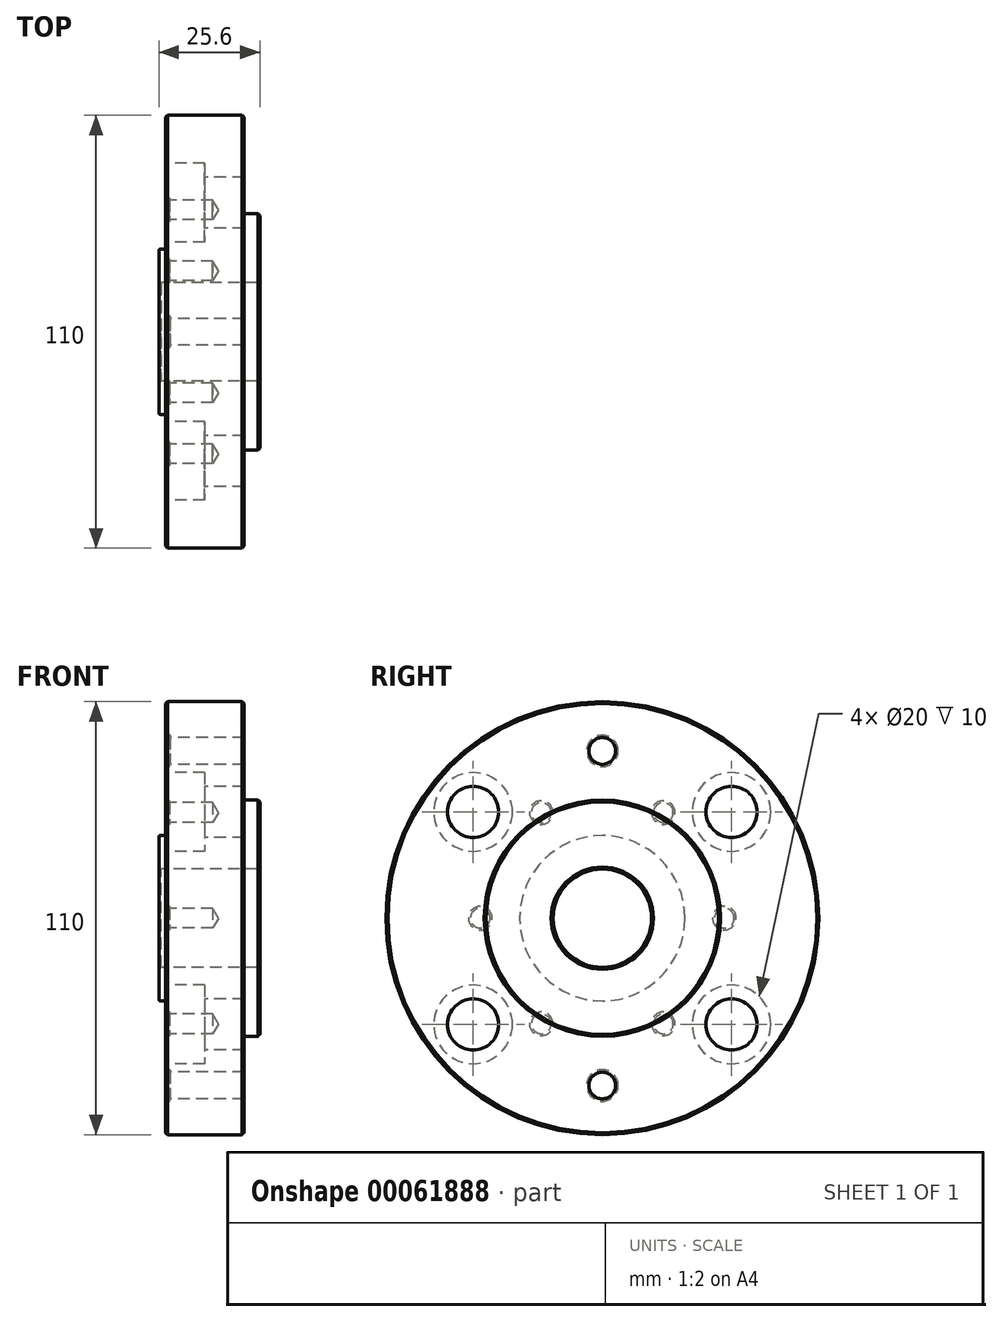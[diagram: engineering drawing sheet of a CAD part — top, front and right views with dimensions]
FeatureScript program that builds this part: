
annotation { "Feature Type Name" : "Feature", "Feature Type Description" : "" }
export const myFeature = defineFeature(function(context is Context, id is Id, definition is map)
    precondition{}
    {
        {
            var Q0;
            Q0=qCreatedBy(makeId("Right.planeOp"),FACE);
            var sketch = newSketch(context, id + "F0", { "sketchPlane" : qUnion([Q0])});
            skCircle(sketch, "E0", {"center": v(0, 0) * mm, "radius": 42.5 * mm, "construction": true});
            skCircle(sketch, "E1", {"center": v(0, 0) * mm, "radius": 21 * mm});
            skCircle(sketch, "E2", {"center": v(0, 0) * mm, "radius": 30 * mm});
            skCircle(sketch, "E3", {"center": v(0, 0) * mm, "radius": 31 * mm, "construction": true});
            skCircle(sketch, "E4", {"center": v(0, 0) * mm, "radius": 55 * mm});
            skPoint(sketch, "E5", {"position": v(-31, 0) * mm});
            skPoint(sketch, "E6", {"position": v(-32.82, -27) * mm});
            skPoint(sketch, "E7", {"position": v(-32.82, 27) * mm});
            skPoint(sketch, "E8", {"position": v(32.82, 27) * mm});
            skPoint(sketch, "E9", {"position": v(32.82, -27) * mm});
            skPoint(sketch, "E10.1.0", {"position": v(-15.5, -26.85) * mm});
            skPoint(sketch, "E10.2.0", {"position": v(15.5, -26.85) * mm});
            skPoint(sketch, "E11.0.3.0", {"position": v(31, 0) * mm});
            skPoint(sketch, "E11.0.4.0", {"position": v(15.5, 26.85) * mm});
            skPoint(sketch, "E11.0.5.0", {"position": v(-15.5, 26.85) * mm});
            skPoint(sketch, "E12", {"position": v(0, -42.5) * mm});
            skPoint(sketch, "E13", {"position": v(0, 42.5) * mm});
            skCircle(sketch, "E14", {"center": v(0, 0) * mm, "radius": 12.5 * mm});
            skSolve(sketch);
        }
        {
            var Q0;
            Q0 = qSketchRegion(id + "F0", true);
            var Q1;
            Q1=makeQuery(id+"F0.imprint","IMPRINT",FACE,{"disambiguationData":[TD([[makeQuery(id+"F0.imprint","IMPRINT",EDGE,{"derivedFrom":sQuery(id+"F0.wireOp",EDGE,"E1")}),1.0]])]});
            var Q2;
            Q2=makeQuery(id+"F0.imprint","IMPRINT",FACE,{"disambiguationData":[TD([[makeQuery(id+"F0.imprint","IMPRINT",EDGE,{"derivedFrom":sQuery(id+"F0.wireOp",EDGE,"E2")}),1.0]])]});
            extrude(context, id + "F1", {"entities" : qUnion([Q0, Q1, Q2]), "depth" : 20 * mm});
        }
        {
            var Q0;
            Q0=makeQuery(id+"F0.imprint","IMPRINT",FACE,{"disambiguationData":[TD([[makeQuery(id+"F0.imprint","IMPRINT",EDGE,{"derivedFrom":sQuery(id+"F0.wireOp",EDGE,"E1")}),1.0]])]});
            var Q1;
            Q1=sQuery(id+"F0.wireOp",EDGE,"E2");
            extrude(context, id + "F2", {"entities" : qUnion([Q0]), "operationType" : NewBodyOperationType.ADD, "surfaceEntities" : qUnion([Q1]), "oppositeDirection" : true, "depth" : 1.6 * mm});
        }
        {
            var Q0;
            Q0=makeQuery(id+"F1.opExtrude","CAP_FACE",FACE,{"disambiguationData":[OSD([sQuery(id+"F0.wireOp",EDGE,"E4")])],"isStart":false});
            var sketch = newSketch(context, id + "F3", { "sketchPlane" : qUnion([Q0])});
            skCircle(sketch, "E15.0", {"center": v(0, 0) * mm, "radius": 30 * mm});
            skSolve(sketch);
        }
        {
            var Q0;
            Q0=makeQuery(id+"F3.imprint","IMPRINT",FACE,{"disambiguationData":[TD([[makeQuery(id+"F3.imprint","IMPRINT",EDGE,{"derivedFrom":sQuery(id+"F3.wireOp",EDGE,"E15.0")}),1.0]])]});
            extrude(context, id + "F4", {"entities" : qUnion([Q0]), "operationType" : NewBodyOperationType.ADD, "depth" : 4 * mm});
        }
        {
            var Q0;
            Q0=sQuery(id+"F0.wireOp",VERTEX,"E11.0.5.0");
            var Q1;
            Q1=sQuery(id+"F0.wireOp",VERTEX,"E5");
            var Q2;
            Q2=sQuery(id+"F0.wireOp",VERTEX,"E10.1.0");
            var Q3;
            Q3=sQuery(id+"F0.wireOp",VERTEX,"E11.0.4.0");
            var Q4;
            Q4=sQuery(id+"F0.wireOp",VERTEX,"E11.0.3.0");
            var Q5;
            Q5=sQuery(id+"F0.wireOp",VERTEX,"E10.2.0");
            var Q6;
            Q6=makeQuery(id+"F1.opExtrude","SWEPT_BODY",BODY,{"disambiguationData":[OSD([sQuery(id+"F0.wireOp",EDGE,"E4")])]});
            hole(context, id + "F5", {"style" : HoleStyle.C_BORE, "holeDiameter" : 5 * mm, "cBoreDiameter" : 6 * mm, "cBoreDepth" : 1 * mm, "endStyle" : HoleEndStyle.BLIND, "oppositeDirection" : true, "holeDepth" : 12 * mm, "locations" : qUnion([Q0, Q1, Q2, Q3, Q4, Q5]), "scope" : qUnion([Q6])});
        }
        {
            var Q0;
            Q0=sQuery(id+"F0.wireOp",VERTEX,"E6");
            var Q1;
            Q1=sQuery(id+"F0.wireOp",VERTEX,"E7");
            var Q2;
            Q2=sQuery(id+"F0.wireOp",VERTEX,"E8");
            var Q3;
            Q3=sQuery(id+"F0.wireOp",VERTEX,"E9");
            var Q4;
            Q4=makeQuery(id+"F1.opExtrude","SWEPT_BODY",BODY,{"disambiguationData":[OSD([sQuery(id+"F0.wireOp",EDGE,"E4")])]});
            hole(context, id + "F6", {"style" : HoleStyle.C_BORE, "holeDiameter" : 13 * mm, "cBoreDiameter" : 20 * mm, "cBoreDepth" : 10 * mm, "endStyle" : HoleEndStyle.THROUGH, "oppositeDirection" : true, "locations" : qUnion([Q0, Q1, Q2, Q3]), "scope" : qUnion([Q4])});
        }
        {
            var Q0;
            Q0=sQuery(id+"F0.wireOp",VERTEX,"E13");
            var Q1;
            Q1=sQuery(id+"F0.wireOp",VERTEX,"E12");
            var Q2;
            Q2=makeQuery(id+"F1.opExtrude","SWEPT_BODY",BODY,{"disambiguationData":[OSD([sQuery(id+"F0.wireOp",EDGE,"E4"),sQuery(id+"F0.wireOp",EDGE,"E14")])]});
            hole(context, id + "F7", {"style" : HoleStyle.C_BORE, "holeDiameter" : 6.8 * mm, "cBoreDiameter" : 8 * mm, "cBoreDepth" : 1.2 * mm, "endStyle" : HoleEndStyle.THROUGH, "oppositeDirection" : true, "locations" : qUnion([Q0, Q1]), "scope" : qUnion([Q2])});
        }
        {
            var Q0;
            Q0=makeQuery(id+"F2.opExtrude","CAP_EDGE",EDGE,{"disambiguationData":[OSD([sQuery(id+"F0.wireOp",EDGE,"E2")])],"isStart":false});
            var Q1;
            Q1=makeQuery(id+"F1.opExtrude","CAP_EDGE",EDGE,{"disambiguationData":[OSD([sQuery(id+"F0.wireOp",EDGE,"E4")])],"isStart":false});
            var Q2;
            Q2=makeQuery(id+"F1.opExtrude","CAP_EDGE",EDGE,{"disambiguationData":[OSD([sQuery(id+"F0.wireOp",EDGE,"E4")])],"isStart":true});
            var Q3;
            Q3=makeQuery(id+"F4.opExtrude","CAP_EDGE",EDGE,{"disambiguationData":[OSD([sQuery(id+"F3.wireOp",EDGE,"E15.0")])],"isStart":false});
            var Q4;
            Q4=makeQuery(id+"F4.opExtrude","CAP_EDGE",EDGE,{"disambiguationData":[OSD([sQuery(id+"F0.wireOp",EDGE,"E14")])],"isStart":false});
            var Q5;
            Q5=makeQuery(id+"F2.opExtrude","CAP_EDGE",EDGE,{"disambiguationData":[OSD([sQuery(id+"F0.wireOp",EDGE,"E14")])],"isStart":false});
            chamfer(context, id + "F8", {"entities" : qUnion([Q0, Q1, Q2, Q3, Q4, Q5]), "chamferType" : ChamferType.OFFSET_ANGLE, "width" : .5 * mm, "oppositeDirection" : false, "angle" : 45 * degree, "tangentPropagation" : true});
        }
        {
            var Q0;
            Q0=makeQuery(id+"F4.opExtrude","CAP_EDGE",EDGE,{"disambiguationData":[OSD([sQuery(id+"F3.wireOp",EDGE,"E15.0")])],"isStart":true});
            var Q1;
            Q1=makeQuery(id+"F2.opExtrude","CAP_EDGE",EDGE,{"disambiguationData":[OSD([sQuery(id+"F0.wireOp",EDGE,"E1")])],"isStart":true});
            var Q2;
            Q2=makeQuery(id+"F2.opExtrude","CAP_EDGE",EDGE,{"disambiguationData":[OSD([sQuery(id+"F0.wireOp",EDGE,"E1")])],"isStart":false});
            fillet(context, id + "F9", {"entities" : qUnion([Q0, Q1, Q2]), "radius" : 0.3 * mm, "tangentPropagation" : true, "allowEdgeOverflow" : false});
        }
    });
